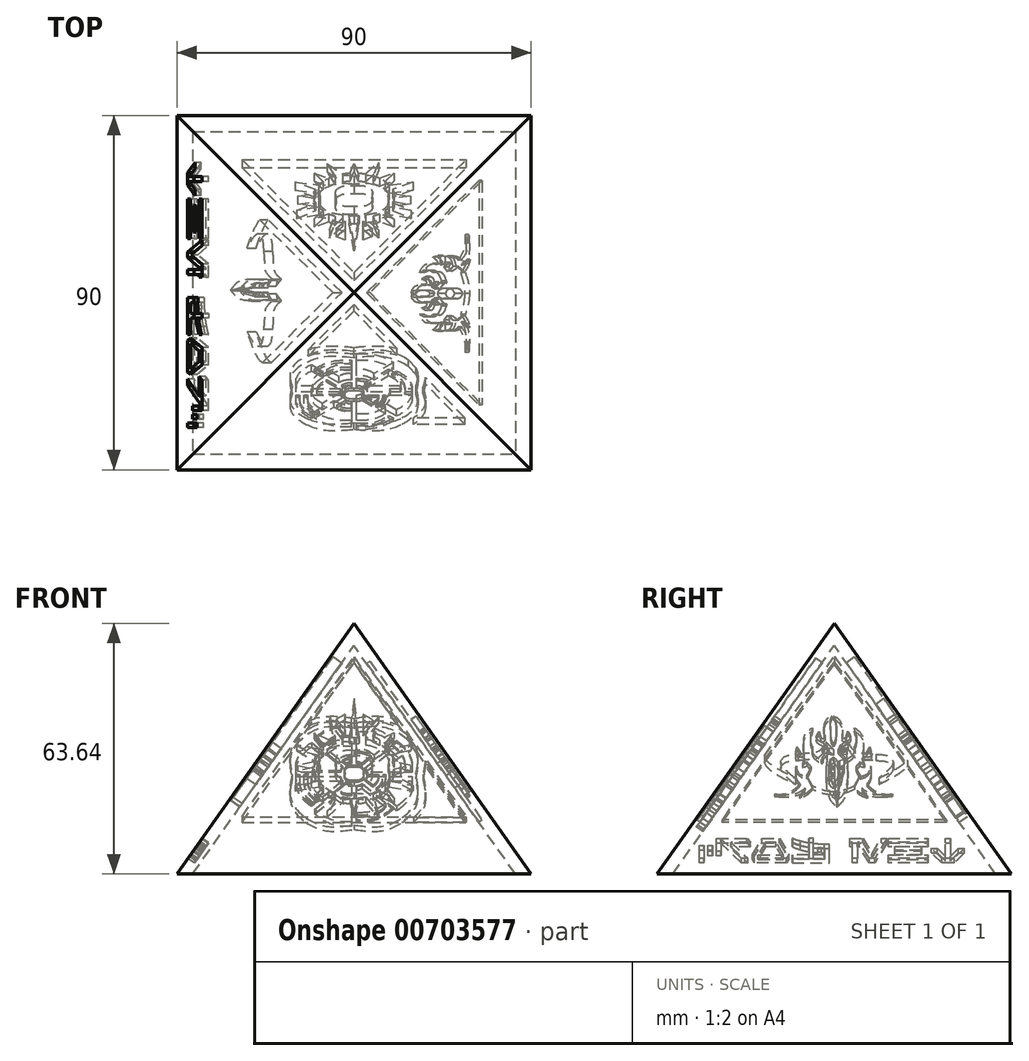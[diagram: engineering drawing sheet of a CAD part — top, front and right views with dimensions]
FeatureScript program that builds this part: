
annotation { "Feature Type Name" : "Feature", "Feature Type Description" : "" }
export const myFeature = defineFeature(function(context is Context, id is Id, definition is map)
    precondition{}
    {
        {
            var Q0;
            Q0=qCreatedBy(makeId("Top.planeOp"),FACE);
            cPlane(context, id + "F0", {"entities" : qUnion([Q0]), "cplaneType" : CPlaneType.OFFSET, "offset" : 63.64 * mm, "width" : 150 * mm, "height" : 150 * mm});
        }
        {
            var Q0;
            Q0=qCreatedBy(id+"F0.planeOp",FACE);
            var sketch = newSketch(context, id + "F1", { "sketchPlane" : qUnion([Q0])});
            skPoint(sketch, "E0", {"position": v(0, 0) * mm});
            skLineSegment(sketch, "E1.bottom", {"start": v(-47.05, 40.97) * mm, "end": v(62.4, 40.97) * mm});
            skLineSegment(sketch, "E1.top", {"start": v(-47.05, -49.65) * mm, "end": v(62.4, -49.65) * mm});
            skLineSegment(sketch, "E1.left", {"start": v(-47.05, 40.97) * mm, "end": v(-47.05, -49.65) * mm});
            skLineSegment(sketch, "E1.right", {"start": v(62.4, 40.97) * mm, "end": v(62.4, -49.65) * mm});
            skSolve(sketch);
        }
        {
            var Q0;
            Q0=qCreatedBy(makeId("Top.planeOp"),FACE);
            var sketch = newSketch(context, id + "F2", { "sketchPlane" : qUnion([Q0])});
            skLineSegment(sketch, "E2.bottom", {"start": v(-45, 45) * mm, "end": v(45, 45) * mm});
            skLineSegment(sketch, "E2.top", {"start": v(-45, -45) * mm, "end": v(45, -45) * mm});
            skLineSegment(sketch, "E2.left", {"start": v(-45, 45) * mm, "end": v(-45, -45) * mm});
            skLineSegment(sketch, "E2.right", {"start": v(45, 45) * mm, "end": v(45, -45) * mm});
            skPoint(sketch, "E3.orphan", {"position": v(-45, 0) * mm});
            skPoint(sketch, "E4.start.orphan", {"position": v(45, 0) * mm});
            skPoint(sketch, "E5.end.orphan", {"position": v(0, -45) * mm});
            skPoint(sketch, "E5.start.orphan", {"position": v(0, 45) * mm});
            skSolve(sketch);
        }
        {
            var Q0;
            Q0=makeQuery(id+"F2.imprint","IMPRINT",FACE,{"disambiguationData":[TD([[makeQuery(id+"F2.imprint","IMPRINT",EDGE,{"derivedFrom":sQuery(id+"F2.wireOp",EDGE,"E2.bottom")}),-1.0]])]});
            var Q1;
            Q1=sQuery(id+"F1.wireOp",VERTEX,"E0");
            loft(context, id + "F3", {"sheetProfilesArray" : [{ "sheetProfileEntities" : qUnion([Q0]) }, { "sheetProfileEntities" : qUnion([Q1]) }]});
        }
        {
            var Q0;
            Q0=qCreatedBy(makeId("Top.planeOp"),FACE);
            cPlane(context, id + "F4", {"entities" : qUnion([Q0]), "cplaneType" : CPlaneType.OFFSET, "offset" : 58 * mm, "width" : 150 * mm, "height" : 150 * mm});
        }
        {
            var Q0;
            Q0=qCreatedBy(id+"F4.planeOp",FACE);
            var sketch = newSketch(context, id + "F5", { "sketchPlane" : qUnion([Q0])});
            skPoint(sketch, "E6", {"position": v(0, 0) * mm});
            skSolve(sketch);
        }
        {
            var Q0;
            Q0=makeQuery(id+"F2.imprint","IMPRINT",FACE,{"disambiguationData":[TD([[makeQuery(id+"F2.imprint","IMPRINT",EDGE,{"derivedFrom":sQuery(id+"F2.wireOp",EDGE,"E2.bottom")}),-1.0]])]});
            var sketch = newSketch(context, id + "F6", { "sketchPlane" : qUnion([Q0])});
            skLineSegment(sketch, "E7.0", {"start": v(-41, 41) * mm, "end": v(-41, -41) * mm});
            skLineSegment(sketch, "E7.1", {"start": v(-41, 41) * mm, "end": v(41, 41) * mm});
            skLineSegment(sketch, "E7.2", {"start": v(41, 41) * mm, "end": v(41, -41) * mm});
            skLineSegment(sketch, "E7.3", {"start": v(-41, -41) * mm, "end": v(41, -41) * mm});
            skSolve(sketch);
        }
        {
            var Q1;
            Q1=makeQuery(id+"F6.imprint","IMPRINT",FACE,{"disambiguationData":[TD([[makeQuery(id+"F6.imprint","IMPRINT",EDGE,{"derivedFrom":sQuery(id+"F6.wireOp",EDGE,"E7.0")}),1.0]])]});
            var Q2;
            Q2=sQuery(id+"F5.wireOp",VERTEX,"E6");
            loft(context, id + "F7", {"operationType" : NewBodyOperationType.REMOVE, "sheetProfilesArray" : [{ "sheetProfileEntities" : qUnion([Q1]) }, { "sheetProfileEntities" : qUnion([Q2]) }]});
        }
        {
            var Q0;
            Q0=makeQuery(id+"F3.opLoft","SWEPT_FACE",FACE,{"disambiguationData":[OSD([sQuery(id+"F2.wireOp",EDGE,"E2.bottom"),sQuery(id+"F2.wireOp",EDGE,"E2.top"),sQuery(id+"F2.wireOp",EDGE,"E2.left")])]});
            var sketch = newSketch(context, id + "F8", { "sketchPlane" : qUnion([Q0])});
            skLineSegment(sketch, "E8", {"start": v(-30.48, -21.2) * mm, "end": v(-27.31, -21.2) * mm});
            skLineSegment(sketch, "E9", {"start": v(-27.31, -21.2) * mm, "end": v(-24.66, -18.07) * mm});
            skLineSegment(sketch, "E10", {"start": v(-24.66, -18.07) * mm, "end": v(-26.25, -18.07) * mm});
            skLineSegment(sketch, "E11", {"start": v(-26.25, -18.07) * mm, "end": v(-28.3, -20.5) * mm});
            skLineSegment(sketch, "E12", {"start": v(-28.3, -20.5) * mm, "end": v(-28.3, -14.95) * mm});
            skLineSegment(sketch, "E13", {"start": v(-28.3, -14.95) * mm, "end": v(-29.48, -14.95) * mm});
            skLineSegment(sketch, "E14", {"start": v(-29.48, -14.95) * mm, "end": v(-29.48, -20.5) * mm});
            skLineSegment(sketch, "E15", {"start": v(-29.48, -20.5) * mm, "end": v(-31.54, -18.07) * mm});
            skLineSegment(sketch, "E16", {"start": v(-31.54, -18.07) * mm, "end": v(-33.13, -18.07) * mm});
            skLineSegment(sketch, "E17", {"start": v(-33.13, -18.07) * mm, "end": v(-30.48, -21.2) * mm});
            skLineSegment(sketch, "E18", {"start": v(-13.74, -16.13) * mm, "end": v(-13.74, -14.95) * mm});
            skLineSegment(sketch, "E19", {"start": v(-13.74, -14.95) * mm, "end": v(-23.85, -14.95) * mm});
            skLineSegment(sketch, "E20", {"start": v(-23.85, -14.95) * mm, "end": v(-23.85, -16.13) * mm});
            skLineSegment(sketch, "E21", {"start": v(-23.85, -16.13) * mm, "end": v(-13.74, -16.13) * mm});
            skLineSegment(sketch, "E22", {"start": v(-13.74, -21.2) * mm, "end": v(-13.74, -20.01) * mm});
            skLineSegment(sketch, "E23", {"start": v(-13.74, -20.01) * mm, "end": v(-23.85, -20.01) * mm});
            skLineSegment(sketch, "E24", {"start": v(-23.85, -20.01) * mm, "end": v(-23.85, -21.2) * mm});
            skLineSegment(sketch, "E25", {"start": v(-23.85, -21.2) * mm, "end": v(-13.74, -21.2) * mm});
            skLineSegment(sketch, "E26", {"start": v(-15.46, -18.66) * mm, "end": v(-15.46, -17.48) * mm});
            skLineSegment(sketch, "E27", {"start": v(-15.46, -17.48) * mm, "end": v(-22.13, -17.48) * mm});
            skLineSegment(sketch, "E28", {"start": v(-22.13, -17.48) * mm, "end": v(-22.13, -18.66) * mm});
            skLineSegment(sketch, "E29", {"start": v(-22.13, -18.66) * mm, "end": v(-15.46, -18.66) * mm});
            skLineSegment(sketch, "E30", {"start": v(-9.62, -19.72) * mm, "end": v(-11.96, -14.95) * mm});
            skLineSegment(sketch, "E31", {"start": v(-11.96, -14.95) * mm, "end": v(-13.4, -14.95) * mm});
            skLineSegment(sketch, "E32", {"start": v(-13.4, -14.95) * mm, "end": v(-10.33, -21.2) * mm});
            skLineSegment(sketch, "E33", {"start": v(-10.33, -21.2) * mm, "end": v(-8.9, -21.2) * mm});
            skLineSegment(sketch, "E34", {"start": v(-8.9, -21.2) * mm, "end": v(-6.42, -16.13) * mm});
            skLineSegment(sketch, "E35", {"start": v(-6.42, -16.13) * mm, "end": v(-5.84, -16.13) * mm});
            skLineSegment(sketch, "E36", {"start": v(-5.84, -16.13) * mm, "end": v(-5.84, -21.2) * mm});
            skLineSegment(sketch, "E37", {"start": v(-5.84, -21.2) * mm, "end": v(-4.66, -21.2) * mm});
            skLineSegment(sketch, "E38", {"start": v(-4.66, -21.2) * mm, "end": v(-4.66, -16.13) * mm});
            skLineSegment(sketch, "E39", {"start": v(-4.66, -16.13) * mm, "end": v(-3.94, -16.13) * mm});
            skLineSegment(sketch, "E40", {"start": v(-3.94, -16.13) * mm, "end": v(-3.94, -14.95) * mm});
            skLineSegment(sketch, "E41", {"start": v(-3.94, -14.95) * mm, "end": v(-7.28, -14.95) * mm});
            skLineSegment(sketch, "E42", {"start": v(-7.28, -14.95) * mm, "end": v(-9.62, -19.72) * mm});
            skLineSegment(sketch, "E43", {"start": v(2.43, -20.01) * mm, "end": v(5.3, -20.01) * mm});
            skLineSegment(sketch, "E44", {"start": v(5.3, -20.01) * mm, "end": v(5.3, -17.82) * mm});
            skLineSegment(sketch, "E45", {"start": v(2.43, -17.95) * mm, "end": v(2.43, -20.01) * mm});
            skLineSegment(sketch, "E46", {"start": v(5.3, -16.6) * mm, "end": v(5.3, -14.95) * mm});
            skLineSegment(sketch, "E47", {"start": v(5.3, -14.95) * mm, "end": v(6.48, -14.95) * mm});
            skLineSegment(sketch, "E48", {"start": v(6.48, -14.95) * mm, "end": v(6.48, -16.4) * mm});
            skLineSegment(sketch, "E49", {"start": v(10.66, -14.95) * mm, "end": v(10.66, -16.14) * mm});
            skLineSegment(sketch, "E50", {"start": v(6.48, -17.65) * mm, "end": v(6.48, -20.01) * mm});
            skLineSegment(sketch, "E51", {"start": v(6.48, -20.01) * mm, "end": v(10.66, -20.01) * mm});
            skLineSegment(sketch, "E52", {"start": v(10.66, -20.01) * mm, "end": v(10.66, -21.2) * mm});
            skLineSegment(sketch, "E53", {"start": v(10.66, -21.2) * mm, "end": v(1.25, -21.2) * mm});
            skLineSegment(sketch, "E54", {"start": v(1.25, -21.2) * mm, "end": v(1.25, -16.76) * mm});
            skLineSegment(sketch, "E55", {"start": v(1.25, -16.76) * mm, "end": v(2.43, -16.76) * mm});
            skLineSegment(sketch, "E56", {"start": v(12.92, -20.01) * mm, "end": v(14.82, -16.13) * mm});
            skLineSegment(sketch, "E57", {"start": v(14.82, -16.13) * mm, "end": v(17.48, -16.13) * mm});
            skLineSegment(sketch, "E58", {"start": v(17.48, -16.13) * mm, "end": v(19.37, -20.01) * mm});
            skLineSegment(sketch, "E59", {"start": v(19.37, -20.01) * mm, "end": v(12.92, -20.01) * mm});
            skLineSegment(sketch, "E60", {"start": v(20.26, -21.2) * mm, "end": v(20.83, -20.04) * mm});
            skLineSegment(sketch, "E61", {"start": v(20.83, -20.04) * mm, "end": v(18.33, -14.95) * mm});
            skLineSegment(sketch, "E62", {"start": v(18.33, -14.95) * mm, "end": v(13.96, -14.95) * mm});
            skLineSegment(sketch, "E63", {"start": v(13.96, -14.95) * mm, "end": v(11.5, -19.98) * mm});
            skLineSegment(sketch, "E64", {"start": v(11.5, -19.98) * mm, "end": v(12.09, -21.2) * mm});
            skLineSegment(sketch, "E65", {"start": v(12.09, -21.2) * mm, "end": v(20.26, -21.2) * mm});
            skLineSegment(sketch, "E66", {"start": v(23.56, -21.2) * mm, "end": v(28.74, -15.1) * mm});
            skLineSegment(sketch, "E67", {"start": v(28.86, -14.95) * mm, "end": v(22.22, -14.95) * mm});
            skLineSegment(sketch, "E68", {"start": v(22.22, -14.95) * mm, "end": v(21.22, -16.13) * mm});
            skLineSegment(sketch, "E69", {"start": v(21.22, -16.13) * mm, "end": v(26.26, -16.13) * mm});
            skLineSegment(sketch, "E70", {"start": v(26.26, -16.13) * mm, "end": v(21.97, -21.2) * mm});
            skLineSegment(sketch, "E71", {"start": v(21.97, -21.2) * mm, "end": v(23.56, -21.2) * mm});
            skLineSegment(sketch, "E72", {"start": v(29.92, -19) * mm, "end": v(29.92, -14.95) * mm});
            skLineSegment(sketch, "E73", {"start": v(29.92, -14.95) * mm, "end": v(28.74, -14.95) * mm});
            skLineSegment(sketch, "E74", {"start": v(28.74, -15.1) * mm, "end": v(28.74, -19) * mm});
            skLineSegment(sketch, "E75", {"start": v(28.74, -19) * mm, "end": v(29.92, -19) * mm});
            skLineSegment(sketch, "E76", {"start": v(34.22, -21.2) * mm, "end": v(34.22, -17.13) * mm});
            skLineSegment(sketch, "E77", {"start": v(34.22, -17.13) * mm, "end": v(33.04, -17.13) * mm});
            skLineSegment(sketch, "E78", {"start": v(33.04, -17.13) * mm, "end": v(33.04, -21.2) * mm});
            skLineSegment(sketch, "E79", {"start": v(33.04, -21.2) * mm, "end": v(34.22, -21.2) * mm});
            skLineSegment(sketch, "E80", {"start": v(32.07, -19) * mm, "end": v(32.07, -17.13) * mm});
            skLineSegment(sketch, "E81", {"start": v(32.07, -17.13) * mm, "end": v(30.89, -17.13) * mm});
            skLineSegment(sketch, "E82", {"start": v(30.89, -17.13) * mm, "end": v(30.89, -19) * mm});
            skLineSegment(sketch, "E83", {"start": v(30.89, -19) * mm, "end": v(32.07, -19) * mm});
            skFitSpline(sketch, "E84", {"points": [v(5.3, -17.82) * mm, v(5.1, -17.85) * mm, v(4.72, -17.9) * mm, v(4.34, -17.92) * mm, v(4.16, -17.93) * mm]});
            skFitSpline(sketch, "E85", {"points": [v(4.16, -17.93) * mm, v(4, -17.94) * mm, v(3.7, -17.95) * mm, v(3.4, -17.96) * mm, v(3.25, -17.96) * mm]});
            skFitSpline(sketch, "E86", {"points": [v(3.25, -17.96) * mm, v(3.1, -17.97) * mm, v(2.83, -17.97) * mm, v(2.56, -17.96) * mm, v(2.43, -17.95) * mm]});
            skFitSpline(sketch, "E87", {"points": [v(2.43, -16.76) * mm, v(2.56, -16.77) * mm, v(2.82, -16.78) * mm, v(3.1, -16.78) * mm, v(3.23, -16.77) * mm]});
            skFitSpline(sketch, "E88", {"points": [v(3.23, -16.77) * mm, v(3.37, -16.77) * mm, v(3.67, -16.76) * mm, v(3.98, -16.74) * mm, v(4.14, -16.73) * mm]});
            skFitSpline(sketch, "E89", {"points": [v(4.14, -16.73) * mm, v(4.33, -16.71) * mm, v(4.71, -16.68) * mm, v(5.1, -16.63) * mm, v(5.3, -16.6) * mm]});
            skFitSpline(sketch, "E90", {"points": [v(6.48, -16.4) * mm, v(6.81, -16.33) * mm, v(7.5, -16.18) * mm, v(8.18, -15.97) * mm, v(8.52, -15.86) * mm]});
            skFitSpline(sketch, "E91", {"points": [v(8.52, -15.86) * mm, v(8.88, -15.74) * mm, v(9.62, -15.48) * mm, v(10.3, -15.13) * mm, v(10.66, -14.95) * mm]});
            skFitSpline(sketch, "E92", {"points": [v(10.66, -16.14) * mm, v(10.33, -16.3) * mm, v(9.66, -16.64) * mm, v(8.96, -16.92) * mm, v(8.6, -17.05) * mm]});
            skFitSpline(sketch, "E93", {"points": [v(8.6, -17.05) * mm, v(8.25, -17.18) * mm, v(7.56, -17.42) * mm, v(6.84, -17.57) * mm, v(6.48, -17.65) * mm]});
            skSolve(sketch);
        }
        {
            var Q0;
            {var subQ3=sQuery(id+"F8.wireOp",EDGE,"E72");Q0=makeQuery(id+"F8.imprint","IMPRINT",FACE,{"disambiguationData":[TD([[makeQuery(id+"F8.imprint","IMPRINT",EDGE,{"derivedFrom":subQ3}),1.0]])]});}
            var Q1;
            Q1=makeQuery(id+"F8.imprint","IMPRINT",FACE,{"disambiguationData":[TD([[makeQuery(id+"F8.imprint","IMPRINT",EDGE,{"derivedFrom":sQuery(id+"F8.wireOp",EDGE,"E80")}),1.0]])]});
            var Q2;
            Q2=makeQuery(id+"F8.imprint","IMPRINT",FACE,{"disambiguationData":[TD([[makeQuery(id+"F8.imprint","IMPRINT",EDGE,{"derivedFrom":sQuery(id+"F8.wireOp",EDGE,"E76")}),1.0]])]});
            var Q3;
            Q3=makeQuery(id+"F8.imprint","IMPRINT",FACE,{"disambiguationData":[TD([[makeQuery(id+"F8.imprint","IMPRINT",EDGE,{"derivedFrom":sQuery(id+"F8.wireOp",EDGE,"E56")}),1.0]])]});
            var Q4;
            Q4=makeQuery(id+"F8.imprint","IMPRINT",FACE,{"disambiguationData":[TD([[makeQuery(id+"F8.imprint","IMPRINT",EDGE,{"derivedFrom":sQuery(id+"F8.wireOp",EDGE,"E43")}),-1.0]])]});
            var Q5;
            Q5=makeQuery(id+"F8.imprint","IMPRINT",FACE,{"disambiguationData":[TD([[makeQuery(id+"F8.imprint","IMPRINT",EDGE,{"derivedFrom":sQuery(id+"F8.wireOp",EDGE,"E30")}),1.0]])]});
            var Q6;
            Q6=makeQuery(id+"F8.imprint","IMPRINT",FACE,{"disambiguationData":[TD([[makeQuery(id+"F8.imprint","IMPRINT",EDGE,{"derivedFrom":sQuery(id+"F8.wireOp",EDGE,"E18")}),1.0]])]});
            var Q7;
            Q7=makeQuery(id+"F8.imprint","IMPRINT",FACE,{"disambiguationData":[TD([[makeQuery(id+"F8.imprint","IMPRINT",EDGE,{"derivedFrom":sQuery(id+"F8.wireOp",EDGE,"E26")}),1.0]])]});
            var Q8;
            Q8=makeQuery(id+"F8.imprint","IMPRINT",FACE,{"disambiguationData":[TD([[makeQuery(id+"F8.imprint","IMPRINT",EDGE,{"derivedFrom":sQuery(id+"F8.wireOp",EDGE,"E22")}),1.0]])]});
            var Q9;
            Q9=makeQuery(id+"F8.imprint","IMPRINT",FACE,{"disambiguationData":[TD([[makeQuery(id+"F8.imprint","IMPRINT",EDGE,{"derivedFrom":sQuery(id+"F8.wireOp",EDGE,"E8")}),1.0]])]});
            extrude(context, id + "F9", {"entities" : qUnion([Q0, Q1, Q2, Q3, Q4, Q5, Q6, Q7, Q8, Q9]), "operationType" : NewBodyOperationType.REMOVE, "oppositeDirection" : true, "depth" : 2 * mm, "offsetDistance" : 25 * mm});
        }
        {
            var Q0;
            Q0=makeQuery(id+"F7.boolean.opBoolean","COPY",FACE,{"derivedFrom":makeQuery(id+"F7.opLoft","SWEPT_FACE",FACE,{"disambiguationData":[OSD([sQuery(id+"F6.wireOp",EDGE,"E7.0"),sQuery(id+"F6.wireOp",EDGE,"E7.1"),sQuery(id+"F6.wireOp",EDGE,"E7.2")])]})});
            var sketch = newSketch(context, id + "F10", { "sketchPlane" : qUnion([Q0])});
            skLineSegment(sketch, "E94", {"start": v(-41, -23.67) * mm, "end": v(0, 47.36) * mm, "construction": true});
            skLineSegment(sketch, "E95", {"start": v(0, 47.36) * mm, "end": v(41, -23.67) * mm, "construction": true});
            skLineSegment(sketch, "E96", {"start": v(41, -23.67) * mm, "end": v(-41, -23.67) * mm, "construction": true});
            skLineSegment(sketch, "E97.0", {"start": v(0, 42.02) * mm, "end": v(28.45, -7.63) * mm});
            skLineSegment(sketch, "E98", {"start": v(-28.45, -7.63) * mm, "end": v(28.45, -7.63) * mm});
            skLineSegment(sketch, "E99.trimOffspring", {"start": v(-28.45, -7.63) * mm, "end": v(0, 42.02) * mm});
            skFitSpline(sketch, "E100", {"points": [v(-1.26, 16.9) * mm, v(-0.84, 16.96) * mm, v(-0.42, 16.99) * mm, v(0.01, 16.99) * mm]});
            skFitSpline(sketch, "E101", {"points": [v(0, 16.99) * mm, v(0.42, 17) * mm, v(0.84, 16.97) * mm, v(1.25, 16.91) * mm]});
            skLineSegment(sketch, "E102", {"start": v(0, 29.1) * mm, "end": v(-1.06, 18.9) * mm});
            skLineSegment(sketch, "E103", {"start": v(1.05, 18.88) * mm, "end": v(0, 29.1) * mm});
            skLineSegment(sketch, "E104", {"start": v(-2.27, 24.2) * mm, "end": v(-4.53, 22.69) * mm});
            skLineSegment(sketch, "E105", {"start": v(-4.53, 22.69) * mm, "end": v(-2.27, 19.3) * mm});
            skLineSegment(sketch, "E106", {"start": v(-2.27, 19.3) * mm, "end": v(-2.27, 24.2) * mm});
            skLineSegment(sketch, "E107", {"start": v(2.27, 24.2) * mm, "end": v(2.27, 19.3) * mm});
            skLineSegment(sketch, "E108", {"start": v(2.27, 19.3) * mm, "end": v(4.53, 22.69) * mm});
            skLineSegment(sketch, "E109", {"start": v(4.53, 22.69) * mm, "end": v(2.27, 24.2) * mm});
            skFitSpline(sketch, "E110", {"points": [v(-4.87, 17.28) * mm, v(-5.41, 16.99) * mm, v(-5.93, 16.64) * mm, v(-6.4, 16.26) * mm]});
            skLineSegment(sketch, "E111", {"start": v(-6.22, 23.35) * mm, "end": v(-4.87, 17.28) * mm});
            skFitSpline(sketch, "E112", {"points": [v(-7.9, 14.76) * mm, v(-8.3, 14.28) * mm, v(-8.66, 13.76) * mm, v(-8.96, 13.2) * mm]});
            skLineSegment(sketch, "E113", {"start": v(-6.4, 16.26) * mm, "end": v(-10.15, 18.49) * mm});
            skLineSegment(sketch, "E114", {"start": v(-10.15, 18.49) * mm, "end": v(-7.9, 14.76) * mm});
            skFitSpline(sketch, "E115", {"points": [v(-9.78, 11.23) * mm, v(-9.96, 10.64) * mm, v(-10.08, 10.02) * mm, v(-10.15, 9.39) * mm]});
            skLineSegment(sketch, "E116", {"start": v(-8.96, 13.2) * mm, "end": v(-14.62, 14.72) * mm});
            skLineSegment(sketch, "E117", {"start": v(-14.62, 14.72) * mm, "end": v(-9.78, 11.23) * mm});
            skFitSpline(sketch, "E118", {"points": [v(-10.15, 7.28) * mm, v(-10.08, 6.66) * mm, v(-9.96, 6.05) * mm, v(-9.78, 5.46) * mm]});
            skLineSegment(sketch, "E119", {"start": v(-10.15, 9.39) * mm, "end": v(-14.35, 8.34) * mm});
            skLineSegment(sketch, "E120", {"start": v(-14.35, 8.34) * mm, "end": v(-10.15, 7.28) * mm});
            skFitSpline(sketch, "E121", {"points": [v(-8.96, 3.46) * mm, v(-8.66, 2.91) * mm, v(-8.3, 2.4) * mm, v(-7.9, 1.91) * mm]});
            skLineSegment(sketch, "E122", {"start": v(-9.78, 5.46) * mm, "end": v(-15, 2.13) * mm});
            skLineSegment(sketch, "E123", {"start": v(-15, 2.13) * mm, "end": v(-8.96, 3.46) * mm});
            skFitSpline(sketch, "E124", {"points": [v(-6.42, 0.43) * mm, v(-5.94, 0.04) * mm, v(-5.42, -0.3) * mm, v(-4.87, -0.6) * mm]});
            skLineSegment(sketch, "E125", {"start": v(-7.9, 1.91) * mm, "end": v(-10.15, -1.8) * mm});
            skLineSegment(sketch, "E126", {"start": v(-10.15, -1.8) * mm, "end": v(-6.42, 0.43) * mm});
            skFitSpline(sketch, "E127", {"points": [v(-2.89, -1.43) * mm, v(-2.3, -1.61) * mm, v(-1.68, -1.73) * mm, v(-1.05, -1.8) * mm]});
            skLineSegment(sketch, "E128", {"start": v(-4.87, -0.6) * mm, "end": v(-6.88, -6.06) * mm});
            skLineSegment(sketch, "E129", {"start": v(-6.88, -6.06) * mm, "end": v(-2.89, -1.43) * mm});
            skFitSpline(sketch, "E130", {"points": [v(1.05, -1.8) * mm, v(1.68, -1.74) * mm, v(2.3, -1.61) * mm, v(2.9, -1.43) * mm]});
            skLineSegment(sketch, "E131", {"start": v(-1.05, -1.8) * mm, "end": v(0, -6.01) * mm});
            skLineSegment(sketch, "E132", {"start": v(0, -6.01) * mm, "end": v(1.05, -1.8) * mm});
            skFitSpline(sketch, "E133", {"points": [v(4.88, -0.62) * mm, v(5.42, -0.32) * mm, v(5.94, 0.03) * mm, v(6.42, 0.42) * mm]});
            skLineSegment(sketch, "E134", {"start": v(2.9, -1.43) * mm, "end": v(6.18, -6.4) * mm});
            skLineSegment(sketch, "E135", {"start": v(6.18, -6.4) * mm, "end": v(4.88, -0.62) * mm});
            skFitSpline(sketch, "E136", {"points": [v(7.92, 1.91) * mm, v(8.31, 2.4) * mm, v(8.66, 2.91) * mm, v(8.96, 3.46) * mm]});
            skLineSegment(sketch, "E137", {"start": v(6.42, 0.42) * mm, "end": v(10.15, -1.8) * mm});
            skLineSegment(sketch, "E138", {"start": v(10.15, -1.8) * mm, "end": v(7.92, 1.91) * mm});
            skFitSpline(sketch, "E139", {"points": [v(9.78, 5.46) * mm, v(9.96, 6.05) * mm, v(10.08, 6.66) * mm, v(10.15, 7.28) * mm]});
            skLineSegment(sketch, "E140", {"start": v(8.96, 3.46) * mm, "end": v(15, 2.13) * mm});
            skLineSegment(sketch, "E141", {"start": v(15, 2.13) * mm, "end": v(9.78, 5.46) * mm});
            skFitSpline(sketch, "E142", {"points": [v(10.15, 9.39) * mm, v(10.08, 10.02) * mm, v(9.96, 10.64) * mm, v(9.78, 11.23) * mm]});
            skLineSegment(sketch, "E143", {"start": v(10.15, 7.28) * mm, "end": v(14.35, 8.34) * mm});
            skLineSegment(sketch, "E144", {"start": v(14.35, 8.34) * mm, "end": v(10.15, 9.39) * mm});
            skFitSpline(sketch, "E145", {"points": [v(8.96, 13.2) * mm, v(8.66, 13.76) * mm, v(8.3, 14.29) * mm, v(7.9, 14.77) * mm]});
            skLineSegment(sketch, "E146", {"start": v(9.78, 11.23) * mm, "end": v(14.52, 14.7) * mm});
            skLineSegment(sketch, "E147", {"start": v(14.52, 14.7) * mm, "end": v(8.96, 13.2) * mm});
            skFitSpline(sketch, "E148", {"points": [v(6.42, 16.26) * mm, v(5.94, 16.65) * mm, v(5.42, 16.98) * mm, v(4.88, 17.28) * mm]});
            skLineSegment(sketch, "E149", {"start": v(7.9, 14.77) * mm, "end": v(10.15, 18.49) * mm});
            skLineSegment(sketch, "E150", {"start": v(10.15, 18.49) * mm, "end": v(6.42, 16.26) * mm});
            skFitSpline(sketch, "E151", {"points": [v(2.89, 16.5) * mm, v(6.25, 15.31) * mm, v(8.66, 12.1) * mm, v(8.66, 8.34) * mm]});
            skFitSpline(sketch, "E152", {"points": [v(8.66, 8.34) * mm, v(8.66, 3.56) * mm, v(4.8, -0.32) * mm, v(0.01, -0.32) * mm]});
            skFitSpline(sketch, "E153", {"points": [v(0.01, -0.32) * mm, v(-4.77, -0.32) * mm, v(-8.66, 3.56) * mm, v(-8.66, 8.34) * mm]});
            skFitSpline(sketch, "E154", {"points": [v(-8.66, 8.34) * mm, v(-8.66, 12.1) * mm, v(-6.25, 15.3) * mm, v(-2.89, 16.48) * mm]});
            skLineSegment(sketch, "E155", {"start": v(4.88, 17.28) * mm, "end": v(6.22, 23.35) * mm});
            skLineSegment(sketch, "E156", {"start": v(6.22, 23.35) * mm, "end": v(2.89, 18.12) * mm});
            skLineSegment(sketch, "E157", {"start": v(2.89, 18.12) * mm, "end": v(2.89, 16.5) * mm});
            skFitSpline(sketch, "E158", {"points": [v(0, 12.87) * mm, v(-2.5, 12.87) * mm, v(-4.53, 10.84) * mm, v(-4.53, 8.34) * mm]});
            skFitSpline(sketch, "E159", {"points": [v(-4.53, 8.34) * mm, v(-4.53, 5.83) * mm, v(-2.5, 3.8) * mm, v(0, 3.8) * mm]});
            skFitSpline(sketch, "E160", {"points": [v(0, 3.8) * mm, v(2.5, 3.8) * mm, v(4.53, 5.83) * mm, v(4.53, 8.34) * mm]});
            skFitSpline(sketch, "E161", {"points": [v(4.53, 8.34) * mm, v(4.53, 10.84) * mm, v(2.5, 12.87) * mm, v(0, 12.87) * mm]});
            skLineSegment(sketch, "E162", {"start": v(-2.89, 16.48) * mm, "end": v(-2.89, 18.12) * mm});
            skLineSegment(sketch, "E163", {"start": v(-2.89, 18.12) * mm, "end": v(-6.22, 23.35) * mm});
            skLineSegment(sketch, "E164", {"start": v(-1.06, 18.9) * mm, "end": v(-1.26, 16.9) * mm});
            skLineSegment(sketch, "E165", {"start": v(1.05, 18.88) * mm, "end": v(1.25, 16.91) * mm});
            skSolve(sketch);
        }
        {
            var Q0;
            Q0=makeQuery(id+"F10.imprint","IMPRINT",FACE,{"disambiguationData":[TD([[makeQuery(id+"F10.imprint","IMPRINT",EDGE,{"derivedFrom":sQuery(id+"F10.wireOp",EDGE,"E115")}),-1.0]])]});
            var Q1;
            Q1=makeQuery(id+"F10.imprint","IMPRINT",FACE,{"disambiguationData":[TD([[makeQuery(id+"F10.imprint","IMPRINT",EDGE,{"derivedFrom":sQuery(id+"F10.wireOp",EDGE,"E133")}),-1.0]])]});
            var Q2;
            Q2=makeQuery(id+"F10.imprint","IMPRINT",FACE,{"disambiguationData":[TD([[makeQuery(id+"F10.imprint","IMPRINT",EDGE,{"derivedFrom":sQuery(id+"F10.wireOp",EDGE,"E127")}),-1.0]])]});
            var Q3;
            Q3=makeQuery(id+"F10.imprint","IMPRINT",FACE,{"disambiguationData":[TD([[makeQuery(id+"F10.imprint","IMPRINT",EDGE,{"derivedFrom":sQuery(id+"F10.wireOp",EDGE,"E104")}),-1.0]])]});
            extrude(context, id + "F11", {"entities" : qUnion([Q0, Q1, Q2, Q3]), "operationType" : NewBodyOperationType.REMOVE, "oppositeDirection" : true, "depth" : 2.5 * mm, "offsetDistance" : 25 * mm});
        }
        {
            var Q0;
            Q0=makeQuery(id+"F7.boolean.opBoolean","COPY",FACE,{"derivedFrom":makeQuery(id+"F7.opLoft","SWEPT_FACE",FACE,{"disambiguationData":[OSD([sQuery(id+"F6.wireOp",EDGE,"E7.0"),sQuery(id+"F6.wireOp",EDGE,"E7.1"),sQuery(id+"F6.wireOp",EDGE,"E7.3")])]})});
            var sketch = newSketch(context, id + "F12", { "sketchPlane" : qUnion([Q0])});
            skLineSegment(sketch, "E166", {"start": v(0, 47.36) * mm, "end": v(41, -23.67) * mm, "construction": true});
            skLineSegment(sketch, "E167", {"start": v(41, -23.67) * mm, "end": v(-41, -23.67) * mm, "construction": true});
            skLineSegment(sketch, "E168.0", {"start": v(0, 42.02) * mm, "end": v(28.45, -7.63) * mm});
            skLineSegment(sketch, "E169", {"start": v(-28.45, -7.63) * mm, "end": v(28.45, -7.63) * mm});
            skLineSegment(sketch, "E170.trimOffspring", {"start": v(-28.45, -7.63) * mm, "end": v(0, 42.02) * mm});
            skFitSpline(sketch, "E171", {"points": [v(-2.96, 21.4) * mm, v(-3.37, 21.37) * mm, v(-3.6, 21.2) * mm, v(-3.6, 20.86) * mm]});
            skFitSpline(sketch, "E172", {"points": [v(-3.6, 20.86) * mm, v(-3.6, 20.02) * mm, v(-2.1, 18.49) * mm, v(-0.2, 17.35) * mm]});
            skFitSpline(sketch, "E173", {"points": [v(-4.91, 20.37) * mm, v(-5.22, 20.4) * mm, v(-5.38, 19.99) * mm, v(-5.44, 19.59) * mm]});
            skFitSpline(sketch, "E174", {"points": [v(-5.44, 19.59) * mm, v(-5.98, 15.78) * mm, v(-7.7, 15.7) * mm, v(-8.98, 15.45) * mm]});
            skFitSpline(sketch, "E175", {"points": [v(-8.98, 15.45) * mm, v(-13.62, 14.55) * mm, v(-17.73, 11.22) * mm, v(-9.88, 4.16) * mm]});
            skFitSpline(sketch, "E176", {"points": [v(-9.88, 4.16) * mm, v(-13.57, 9.03) * mm, v(-12.2, 11.06) * mm, v(-9.21, 11.58) * mm]});
            skFitSpline(sketch, "E177", {"points": [v(-9.21, 11.58) * mm, v(-6.9, 11.98) * mm, v(-4, 12.53) * mm, v(-2.06, 15.37) * mm]});
            skLineSegment(sketch, "E178", {"start": v(-0.48, 14.3) * mm, "end": v(-4.91, 20.37) * mm});
            skFitSpline(sketch, "E179", {"points": [v(-1.78, 13.57) * mm, v(-1.57, 0.89) * mm, v(-0.04, -2.03) * mm, v(0.58, -2.7) * mm]});
            skFitSpline(sketch, "E180", {"points": [v(0.58, -2.7) * mm, v(0.63, -2.75) * mm, v(0.67, -2.8) * mm, v(0.7, -2.82) * mm]});
            skFitSpline(sketch, "E181", {"points": [v(0.7, -2.82) * mm, v(0.75, -2.8) * mm, v(0.79, -2.75) * mm, v(0.84, -2.7) * mm]});
            skFitSpline(sketch, "E182", {"points": [v(0.84, -2.7) * mm, v(1.46, -2.03) * mm, v(2.98, 0.9) * mm, v(3.2, 13.57) * mm]});
            skLineSegment(sketch, "E183", {"start": v(-2.06, 15.37) * mm, "end": v(-0.26, 13.12) * mm});
            skLineSegment(sketch, "E184", {"start": v(-0.26, 13.12) * mm, "end": v(-1.78, 13.57) * mm});
            skFitSpline(sketch, "E185", {"points": [v(3.48, 15.37) * mm, v(5.42, 12.53) * mm, v(8.32, 11.98) * mm, v(10.63, 11.58) * mm]});
            skFitSpline(sketch, "E186", {"points": [v(10.63, 11.58) * mm, v(13.62, 11.06) * mm, v(14.98, 9.03) * mm, v(11.3, 4.16) * mm]});
            skFitSpline(sketch, "E187", {"points": [v(11.3, 4.16) * mm, v(19.15, 11.22) * mm, v(15.04, 14.55) * mm, v(10.4, 15.45) * mm]});
            skFitSpline(sketch, "E188", {"points": [v(10.4, 15.45) * mm, v(9.12, 15.7) * mm, v(7.4, 15.78) * mm, v(6.85, 19.59) * mm]});
            skFitSpline(sketch, "E189", {"points": [v(6.85, 19.58) * mm, v(6.8, 19.98) * mm, v(6.64, 20.39) * mm, v(6.33, 20.37) * mm]});
            skLineSegment(sketch, "E190", {"start": v(3.2, 13.57) * mm, "end": v(1.67, 13.12) * mm});
            skLineSegment(sketch, "E191", {"start": v(1.67, 13.12) * mm, "end": v(3.48, 15.37) * mm});
            skFitSpline(sketch, "E192", {"points": [v(1.62, 17.35) * mm, v(3.52, 18.49) * mm, v(5.02, 20.02) * mm, v(5.02, 20.86) * mm]});
            skFitSpline(sketch, "E193", {"points": [v(5.02, 20.86) * mm, v(5.02, 21.25) * mm, v(4.71, 21.42) * mm, v(4.19, 21.4) * mm]});
            skFitSpline(sketch, "E194", {"points": [v(4.19, 21.4) * mm, v(3.52, 21.37) * mm, v(2.5, 21.02) * mm, v(1.36, 20.37) * mm]});
            skLineSegment(sketch, "E195", {"start": v(6.33, 20.37) * mm, "end": v(1.9, 14.3) * mm});
            skFitSpline(sketch, "E196", {"points": [v(0.05, 20.37) * mm, v(-1.08, 21.02) * mm, v(-2.1, 21.37) * mm, v(-2.77, 21.4) * mm]});
            skFitSpline(sketch, "E197", {"points": [v(-2.77, 21.4) * mm, v(-2.84, 21.4) * mm, v(-2.9, 21.4) * mm, v(-2.96, 21.4) * mm]});
            skLineSegment(sketch, "E198", {"start": v(1.36, 20.37) * mm, "end": v(1.36, 17.2) * mm});
            skLineSegment(sketch, "E199", {"start": v(1.36, 17.2) * mm, "end": v(1.36, 13.57) * mm});
            skLineSegment(sketch, "E200", {"start": v(1.36, 13.57) * mm, "end": v(1.36, 13.03) * mm});
            skLineSegment(sketch, "E201", {"start": v(1.36, 13.03) * mm, "end": v(0.05, 13.03) * mm});
            skLineSegment(sketch, "E202", {"start": v(0.05, 13.03) * mm, "end": v(0.05, 13.57) * mm});
            skLineSegment(sketch, "E203", {"start": v(0.05, 13.57) * mm, "end": v(0.05, 17.2) * mm});
            skLineSegment(sketch, "E204", {"start": v(0.05, 17.2) * mm, "end": v(0.05, 20.37) * mm});
            skFitSpline(sketch, "E205", {"points": [v(0.05, 9.55) * mm, v(0.06, 8.7) * mm, v(0.07, 7.94) * mm, v(0.09, 7.22) * mm]});
            skLineSegment(sketch, "E206", {"start": v(-1, 10.17) * mm, "end": v(0.05, 9.55) * mm});
            skLineSegment(sketch, "E207", {"start": v(0.09, 7.22) * mm, "end": v(-1, 8.08) * mm});
            skLineSegment(sketch, "E208", {"start": v(-1, 8.08) * mm, "end": v(-1, 10.17) * mm});
            skFitSpline(sketch, "E209", {"points": [v(1.33, 7.22) * mm, v(1.34, 7.94) * mm, v(1.36, 8.7) * mm, v(1.36, 9.55) * mm]});
            skLineSegment(sketch, "E210", {"start": v(2.4, 10.17) * mm, "end": v(2.4, 8.08) * mm});
            skLineSegment(sketch, "E211", {"start": v(2.4, 8.08) * mm, "end": v(1.33, 7.22) * mm});
            skLineSegment(sketch, "E212", {"start": v(1.36, 9.55) * mm, "end": v(2.4, 10.17) * mm});
            skFitSpline(sketch, "E213", {"points": [v(0.1, 6.68) * mm, v(0.05, 3.98) * mm, v(0.42, 1.05) * mm, v(0.58, -1.77) * mm]});
            skLineSegment(sketch, "E214", {"start": v(-1, 7.56) * mm, "end": v(0.1, 6.68) * mm});
            skFitSpline(sketch, "E215", {"points": [v(0.84, -1.77) * mm, v(1.1, 1.1) * mm, v(1.36, 3.98) * mm, v(1.32, 6.68) * mm]});
            skLineSegment(sketch, "E216", {"start": v(1.32, 6.68) * mm, "end": v(2.4, 7.56) * mm});
            skLineSegment(sketch, "E217", {"start": v(-1, 7.56) * mm, "end": v(0.58, -1.77) * mm});
            skLineSegment(sketch, "E218", {"start": v(0.84, -1.77) * mm, "end": v(2.4, 7.56) * mm});
            skLineSegment(sketch, "E219", {"start": v(0.05, 13.03) * mm, "end": v(-0.26, 13.12) * mm});
            skLineSegment(sketch, "E220", {"start": v(1.36, 13.03) * mm, "end": v(1.67, 13.12) * mm});
            skLineSegment(sketch, "E221", {"start": v(-0.48, 17.52) * mm, "end": v(-0.48, 14.3) * mm});
            skLineSegment(sketch, "E222", {"start": v(1.9, 17.52) * mm, "end": v(1.9, 14.3) * mm});
            skLineSegment(sketch, "E223", {"start": v(0, 47.36) * mm, "end": v(-41, -23.67) * mm, "construction": true});
            skSolve(sketch);
        }
        {
            var Q0;
            Q0=makeQuery(id+"F12.imprint","IMPRINT",FACE,{"disambiguationData":[TD([[makeQuery(id+"F12.imprint","IMPRINT",EDGE,{"derivedFrom":sQuery(id+"F12.wireOp",EDGE,"E171")}),1.0]])]});
            var Q1;
            Q1=makeQuery(id+"F12.imprint","IMPRINT",FACE,{"disambiguationData":[TD([[makeQuery(id+"F12.imprint","IMPRINT",EDGE,{"derivedFrom":sQuery(id+"F12.wireOp",EDGE,"E185")}),1.0]])]});
            var Q2;
            Q2=makeQuery(id+"F12.imprint","IMPRINT",FACE,{"disambiguationData":[TD([[makeQuery(id+"F12.imprint","IMPRINT",EDGE,{"derivedFrom":sQuery(id+"F12.wireOp",EDGE,"E179")}),1.0]])]});
            extrude(context, id + "F13", {"entities" : qUnion([Q0, Q1, Q2]), "operationType" : NewBodyOperationType.REMOVE, "oppositeDirection" : true, "depth" : 2.75 * mm, "offsetDistance" : 25 * mm});
        }
        {
            var Q0;
            Q0=makeQuery(id+"F7.boolean.opBoolean","COPY",FACE,{"derivedFrom":makeQuery(id+"F7.opLoft","SWEPT_FACE",FACE,{"disambiguationData":[OSD([sQuery(id+"F6.wireOp",EDGE,"E7.1"),sQuery(id+"F6.wireOp",EDGE,"E7.2"),sQuery(id+"F6.wireOp",EDGE,"E7.3")])]})});
            var sketch = newSketch(context, id + "F14", { "sketchPlane" : qUnion([Q0])});
            skLineSegment(sketch, "E224", {"start": v(-41, -23.67) * mm, "end": v(0, 47.36) * mm, "construction": true});
            skLineSegment(sketch, "E225", {"start": v(0, 47.36) * mm, "end": v(41, -23.67) * mm, "construction": true});
            skLineSegment(sketch, "E226", {"start": v(41, -23.67) * mm, "end": v(-41, -23.67) * mm, "construction": true});
            skLineSegment(sketch, "E227.0", {"start": v(0, 41.8) * mm, "end": v(28.51, -7.6) * mm});
            skLineSegment(sketch, "E228", {"start": v(-28.51, -7.6) * mm, "end": v(28.51, -7.6) * mm});
            skLineSegment(sketch, "E229.trimOffspring", {"start": v(-28.51, -7.6) * mm, "end": v(0, 41.8) * mm});
            skFitSpline(sketch, "E230", {"points": [v(8.78, -0.88) * mm, v(8.2, -0.15) * mm, v(7.74, 0.72) * mm, v(7.4, 1.66) * mm]});
            skFitSpline(sketch, "E231", {"points": [v(7.4, 1.66) * mm, v(8.79, 0.33) * mm, v(10.83, -0.52) * mm, v(13.1, -0.52) * mm]});
            skFitSpline(sketch, "E232", {"points": [v(13.1, -0.52) * mm, v(13.82, -0.52) * mm, v(14.53, -0.43) * mm, v(15.2, -0.27) * mm]});
            skFitSpline(sketch, "E233", {"points": [v(15.2, -0.27) * mm, v(12.68, -0.17) * mm, v(10.4, 1.02) * mm, v(8.65, 2.92) * mm]});
            skFitSpline(sketch, "E234", {"points": [v(8.65, 2.92) * mm, v(9.28, 3.83) * mm, v(9.69, 5.44) * mm, v(9.69, 7.27) * mm]});
            skFitSpline(sketch, "E235", {"points": [v(9.69, 7.27) * mm, v(9.69, 7.69) * mm, v(9.67, 8.09) * mm, v(9.63, 8.47) * mm]});
            skFitSpline(sketch, "E236", {"points": [v(9.63, 8.47) * mm, v(9.38, 6.97) * mm, v(8.38, 5.73) * mm, v(7.04, 5.17) * mm]});
            skFitSpline(sketch, "E237", {"points": [v(7.04, 5.17) * mm, v(6.56, 6.02) * mm, v(6.17, 6.96) * mm, v(5.88, 7.95) * mm]});
            skFitSpline(sketch, "E238", {"points": [v(5.88, 7.95) * mm, v(6.28, 8.37) * mm, v(6.62, 8.83) * mm, v(6.9, 9.33) * mm]});
            skFitSpline(sketch, "E239", {"points": [v(6.9, 9.33) * mm, v(7.25, 8.97) * mm, v(7.5, 8.73) * mm, v(8.01, 8.7) * mm]});
            skFitSpline(sketch, "E240", {"points": [v(8.01, 8.7) * mm, v(7.74, 10.92) * mm, v(9.44, 10.92) * mm, v(9.44, 14.09) * mm]});
            skFitSpline(sketch, "E241", {"points": [v(9.44, 14.09) * mm, v(8.96, 13.11) * mm, v(8.23, 11.9) * mm, v(7.73, 12.1) * mm]});
            skFitSpline(sketch, "E242", {"points": [v(7.73, 12.1) * mm, v(7.74, 12.24) * mm, v(7.74, 12.37) * mm, v(7.74, 12.5) * mm]});
            skFitSpline(sketch, "E243", {"points": [v(7.74, 12.5) * mm, v(7.74, 15.64) * mm, v(7.25, 18.23) * mm, v(5.55, 19.93) * mm]});
            skFitSpline(sketch, "E244", {"points": [v(5.55, 19.93) * mm, v(5.8, 18.71) * mm, v(6.04, 18.14) * mm, v(6.04, 16.86) * mm]});
            skFitSpline(sketch, "E245", {"points": [v(6.04, 16.86) * mm, v(6.04, 15.87) * mm, v(5.86, 14.93) * mm, v(5.55, 14.07) * mm]});
            skFitSpline(sketch, "E246", {"points": [v(5.55, 14.07) * mm, v(5.54, 12.48) * mm, v(4.67, 11.1) * mm, v(3.38, 10.18) * mm]});
            skFitSpline(sketch, "E247", {"points": [v(3.38, 10.18) * mm, v(3.1, 9.97) * mm, v(2.87, 10.19) * mm, v(3.09, 10.6) * mm]});
            skFitSpline(sketch, "E248", {"points": [v(3.09, 10.6) * mm, v(2.63, 11.4) * mm, v(2.14, 12.14) * mm, v(1.34, 13.15) * mm]});
            skFitSpline(sketch, "E249", {"points": [v(1.34, 13.15) * mm, v(1.51, 13.46) * mm, v(1.76, 14.2) * mm, v(1.9, 14.58) * mm]});
            skFitSpline(sketch, "E250", {"points": [v(1.9, 14.58) * mm, v(2.39, 14.33) * mm, v(2.87, 13.36) * mm, v(3.12, 13.6) * mm]});
            skFitSpline(sketch, "E251", {"points": [v(3.12, 13.53) * mm, v(2.39, 14.75) * mm, v(4.33, 16.45) * mm, v(3.85, 18.89) * mm]});
            skFitSpline(sketch, "E252", {"points": [v(3.85, 18.89) * mm, v(3.6, 17.91) * mm, v(3.12, 16.7) * mm, v(2.37, 17) * mm]});
            skFitSpline(sketch, "E253", {"points": [v(2.37, 17) * mm, v(2.38, 17.23) * mm, v(2.39, 17.45) * mm, v(2.39, 17.67) * mm]});
            skFitSpline(sketch, "E254", {"points": [v(2.39, 17.67) * mm, v(2.54, 20.43) * mm, v(1.74, 22.82) * mm, v(0.52, 23.62) * mm]});
            skFitSpline(sketch, "E255", {"points": [v(0.52, 23.63) * mm, v(0.9, 23.07) * mm, v(1.08, 21.4) * mm, v(0.93, 19.44) * mm]});
            skFitSpline(sketch, "E256", {"points": [v(0.93, 19.44) * mm, v(0.93, 17.48) * mm, v(0.62, 15.83) * mm, v(0.2, 15.3) * mm]});
            skFitSpline(sketch, "E257", {"points": [v(0.2, 15.3) * mm, v(-0.23, 15.83) * mm, v(-0.53, 17.48) * mm, v(-0.53, 19.44) * mm]});
            skFitSpline(sketch, "E258", {"points": [v(-0.53, 19.44) * mm, v(-0.54, 21.4) * mm, v(-0.23, 23.06) * mm, v(0.2, 23.58) * mm]});
            skFitSpline(sketch, "E259", {"points": [v(0.2, 23.58) * mm, v(-1.07, 22.84) * mm, v(-2, 20.5) * mm, v(-2, 17.74) * mm]});
            skFitSpline(sketch, "E260", {"points": [v(-2, 17.74) * mm, v(-2, 17.52) * mm, v(-2, 17.3) * mm, v(-1.98, 17.08) * mm]});
            skFitSpline(sketch, "E261", {"points": [v(-1.98, 17.08) * mm, v(-2.73, 16.76) * mm, v(-3.21, 17.98) * mm, v(-3.46, 18.96) * mm]});
            skFitSpline(sketch, "E262", {"points": [v(-3.46, 18.96) * mm, v(-3.94, 16.52) * mm, v(-2, 14.82) * mm, v(-2.73, 13.6) * mm]});
            skFitSpline(sketch, "E263", {"points": [v(-2.73, 13.6) * mm, v(-2.48, 13.36) * mm, v(-2, 14.33) * mm, v(-1.5, 14.58) * mm]});
            skFitSpline(sketch, "E264", {"points": [v(-1.5, 14.58) * mm, v(-1.37, 14.2) * mm, v(-1.12, 13.46) * mm, v(-0.95, 13.15) * mm]});
            skFitSpline(sketch, "E265", {"points": [v(-0.95, 13.15) * mm, v(-1.75, 12.14) * mm, v(-2.24, 11.4) * mm, v(-2.7, 10.6) * mm]});
            skFitSpline(sketch, "E266", {"points": [v(-2.7, 10.6) * mm, v(-2.48, 10.19) * mm, v(-2.7, 9.97) * mm, v(-3, 10.18) * mm]});
            skFitSpline(sketch, "E267", {"points": [v(-3, 10.18) * mm, v(-4.28, 11.1) * mm, v(-5.15, 12.48) * mm, v(-5.16, 14.07) * mm]});
            skFitSpline(sketch, "E268", {"points": [v(-5.16, 14.07) * mm, v(-5.47, 14.93) * mm, v(-5.65, 15.87) * mm, v(-5.65, 16.86) * mm]});
            skFitSpline(sketch, "E269", {"points": [v(-5.65, 16.86) * mm, v(-5.65, 18.14) * mm, v(-5.4, 18.71) * mm, v(-5.16, 19.93) * mm]});
            skFitSpline(sketch, "E270", {"points": [v(-5.16, 19.93) * mm, v(-6.86, 18.23) * mm, v(-7.35, 15.64) * mm, v(-7.35, 12.5) * mm]});
            skFitSpline(sketch, "E271", {"points": [v(-7.35, 12.5) * mm, v(-7.35, 12.37) * mm, v(-7.35, 12.24) * mm, v(-7.34, 12.1) * mm]});
            skFitSpline(sketch, "E272", {"points": [v(-7.34, 12.1) * mm, v(-7.84, 11.9) * mm, v(-8.57, 13.11) * mm, v(-9.05, 14.09) * mm]});
            skFitSpline(sketch, "E273", {"points": [v(-9.05, 14.09) * mm, v(-9.05, 10.92) * mm, v(-7.35, 10.92) * mm, v(-7.62, 8.7) * mm]});
            skFitSpline(sketch, "E274", {"points": [v(-7.62, 8.7) * mm, v(-7.1, 8.73) * mm, v(-6.86, 8.97) * mm, v(-6.51, 9.33) * mm]});
            skFitSpline(sketch, "E275", {"points": [v(-6.51, 9.33) * mm, v(-6.23, 8.83) * mm, v(-5.9, 8.37) * mm, v(-5.5, 7.95) * mm]});
            skFitSpline(sketch, "E276", {"points": [v(-5.5, 7.95) * mm, v(-5.78, 6.96) * mm, v(-6.17, 6.02) * mm, v(-6.65, 5.17) * mm]});
            skFitSpline(sketch, "E277", {"points": [v(-6.65, 5.17) * mm, v(-7.99, 5.73) * mm, v(-8.99, 6.97) * mm, v(-9.24, 8.47) * mm]});
            skFitSpline(sketch, "E278", {"points": [v(-9.24, 8.47) * mm, v(-9.28, 8.09) * mm, v(-9.3, 7.69) * mm, v(-9.3, 7.27) * mm]});
            skFitSpline(sketch, "E279", {"points": [v(-9.3, 7.27) * mm, v(-9.3, 5.44) * mm, v(-8.89, 3.83) * mm, v(-8.26, 2.92) * mm]});
            skFitSpline(sketch, "E280", {"points": [v(-8.26, 2.92) * mm, v(-10, 1.02) * mm, v(-12.3, -0.17) * mm, v(-14.8, -0.27) * mm]});
            skFitSpline(sketch, "E281", {"points": [v(-14.8, -0.27) * mm, v(-14.14, -0.43) * mm, v(-13.43, -0.52) * mm, v(-12.7, -0.52) * mm]});
            skFitSpline(sketch, "E282", {"points": [v(-12.7, -0.52) * mm, v(-10.44, -0.52) * mm, v(-8.4, 0.33) * mm, v(-7.02, 1.66) * mm]});
            skFitSpline(sketch, "E283", {"points": [v(-7.02, 1.66) * mm, v(-7.35, 0.72) * mm, v(-7.81, -0.15) * mm, v(-8.4, -0.88) * mm]});
            skFitSpline(sketch, "E284", {"points": [v(-8.4, -0.88) * mm, v(-7.06, -0.23) * mm, v(-5.96, 0.7) * mm, v(-5.08, 1.87) * mm]});
            skFitSpline(sketch, "E285", {"points": [v(-5.08, 1.87) * mm, v(-3.36, 0.95) * mm, v(-1.6, 0.35) * mm, v(0.2, 0.08) * mm]});
            skFitSpline(sketch, "E286", {"points": [v(0.2, 0.08) * mm, v(2, 0.35) * mm, v(3.75, 0.95) * mm, v(5.47, 1.87) * mm]});
            skFitSpline(sketch, "E287", {"points": [v(5.47, 1.87) * mm, v(6.35, 0.7) * mm, v(7.45, -0.23) * mm, v(8.78, -0.88) * mm]});
            skFitSpline(sketch, "E288", {"points": [v(0.2, 3.01) * mm, v(-0.51, 3.57) * mm, v(-1.02, 5.08) * mm, v(-1.02, 6.85) * mm]});
            skFitSpline(sketch, "E289", {"points": [v(-1.02, 6.85) * mm, v(-1.02, 8.62) * mm, v(-0.51, 10.12) * mm, v(0.2, 10.68) * mm]});
            skFitSpline(sketch, "E290", {"points": [v(0.2, 10.68) * mm, v(0.9, 10.12) * mm, v(1.41, 8.62) * mm, v(1.41, 6.85) * mm]});
            skFitSpline(sketch, "E291", {"points": [v(1.41, 6.85) * mm, v(1.41, 5.08) * mm, v(0.9, 3.57) * mm, v(0.2, 3.01) * mm]});
            skLineSegment(sketch, "E292", {"start": v(-5.5, 7.95) * mm, "end": v(-3, 10.18) * mm});
            skLineSegment(sketch, "E293", {"start": v(3.38, 10.18) * mm, "end": v(5.88, 7.95) * mm});
            skLineSegment(sketch, "E294", {"start": v(-5.08, 1.87) * mm, "end": v(-6.65, 5.17) * mm});
            skLineSegment(sketch, "E295", {"start": v(5.47, 1.87) * mm, "end": v(7.04, 5.17) * mm});
            skSolve(sketch);
        }
        {
            var Q0;
            Q0=makeQuery(id+"F14.imprint","IMPRINT",FACE,{"disambiguationData":[TD([[makeQuery(id+"F14.imprint","IMPRINT",EDGE,{"derivedFrom":sQuery(id+"F14.wireOp",EDGE,"E267")}),1.0]])]});
            var Q1;
            Q1=makeQuery(id+"F14.imprint","IMPRINT",FACE,{"disambiguationData":[TD([[makeQuery(id+"F14.imprint","IMPRINT",EDGE,{"derivedFrom":sQuery(id+"F14.wireOp",EDGE,"E238")}),1.0]])]});
            var Q2;
            Q2=makeQuery(id+"F14.imprint","IMPRINT",FACE,{"disambiguationData":[TD([[makeQuery(id+"F14.imprint","IMPRINT",EDGE,{"derivedFrom":sQuery(id+"F14.wireOp",EDGE,"E237")}),1.0]])]});
            extrude(context, id + "F15", {"entities" : qUnion([Q0, Q1, Q2]), "operationType" : NewBodyOperationType.REMOVE, "oppositeDirection" : true, "depth" : 2.5 * mm, "offsetDistance" : 25 * mm});
        }
        {
            var Q0;
            Q0=makeQuery(id+"F14.imprint","IMPRINT",FACE,{"disambiguationData":[TD([[makeQuery(id+"F14.imprint","IMPRINT",EDGE,{"derivedFrom":sQuery(id+"F14.wireOp",EDGE,"E277")}),1.0]])]});
            var Q1;
            Q1=makeQuery(id+"F14.imprint","IMPRINT",FACE,{"disambiguationData":[TD([[makeQuery(id+"F14.imprint","IMPRINT",EDGE,{"derivedFrom":sQuery(id+"F14.wireOp",EDGE,"E230")}),1.0]])]});
            extrude(context, id + "F16", {"entities" : qUnion([Q0, Q1]), "operationType" : NewBodyOperationType.REMOVE, "oppositeDirection" : true, "depth" : 2 * mm, "offsetDistance" : 25 * mm});
        }
        {
            var Q0;
            Q0=makeQuery(id+"F7.boolean.opBoolean","COPY",FACE,{"derivedFrom":makeQuery(id+"F7.opLoft","SWEPT_FACE",FACE,{"disambiguationData":[OSD([sQuery(id+"F6.wireOp",EDGE,"E7.0"),sQuery(id+"F6.wireOp",EDGE,"E7.2"),sQuery(id+"F6.wireOp",EDGE,"E7.3")])]})});
            var sketch = newSketch(context, id + "F17", { "sketchPlane" : qUnion([Q0])});
            skFitSpline(sketch, "E296", {"points": [v(0, 23.34) * mm, v(-9.66, 23.34) * mm, v(-17.5, 15.5) * mm, v(-17.5, 5.84) * mm]});
            skFitSpline(sketch, "E297", {"points": [v(-17.5, 5.84) * mm, v(-17.5, -3.82) * mm, v(-9.66, -11.66) * mm, v(0, -11.66) * mm]});
            skFitSpline(sketch, "E298", {"points": [v(0, -11.66) * mm, v(9.66, -11.66) * mm, v(17.5, -3.82) * mm, v(17.5, 5.84) * mm]});
            skFitSpline(sketch, "E299", {"points": [v(17.5, 5.84) * mm, v(17.5, 15.5) * mm, v(9.66, 23.34) * mm, v(0, 23.34) * mm]});
            skFitSpline(sketch, "E300", {"points": [v(0, 21.54) * mm, v(8.66, 21.54) * mm, v(15.7, 14.5) * mm, v(15.7, 5.84) * mm]});
            skFitSpline(sketch, "E301", {"points": [v(15.7, 5.84) * mm, v(15.7, -2.82) * mm, v(8.66, -9.85) * mm, v(0, -9.85) * mm]});
            skFitSpline(sketch, "E302", {"points": [v(0, -9.85) * mm, v(-8.66, -9.85) * mm, v(-15.7, -2.82) * mm, v(-15.7, 5.84) * mm]});
            skFitSpline(sketch, "E303", {"points": [v(-15.7, 5.84) * mm, v(-15.7, 14.5) * mm, v(-8.66, 21.54) * mm, v(0, 21.54) * mm]});
            skFitSpline(sketch, "E304", {"points": [v(-0.58, 20.56) * mm, v(-4.2, 20.42) * mm, v(-7.5, 18.96) * mm, v(-10, 16.66) * mm]});
            skFitSpline(sketch, "E305", {"points": [v(-5.15, 11.81) * mm, v(-3.83, 12.96) * mm, v(-2.3, 13.6) * mm, v(-0.58, 13.7) * mm]});
            skLineSegment(sketch, "E306", {"start": v(-10, 16.66) * mm, "end": v(-5.15, 11.81) * mm});
            skLineSegment(sketch, "E307", {"start": v(-0.58, 13.7) * mm, "end": v(-0.58, 20.56) * mm});
            skFitSpline(sketch, "E308", {"points": [v(0.58, 17.32) * mm, v(3.31, 17.2) * mm, v(5.69, 16.21) * mm, v(7.7, 14.37) * mm]});
            skLineSegment(sketch, "E309", {"start": v(0.58, 20.56) * mm, "end": v(0.58, 17.32) * mm});
            skFitSpline(sketch, "E310", {"points": [v(9.99, 16.66) * mm, v(7.5, 18.96) * mm, v(4.2, 20.41) * mm, v(0.58, 20.56) * mm]});
            skLineSegment(sketch, "E311", {"start": v(7.7, 14.37) * mm, "end": v(9.99, 16.66) * mm});
            skFitSpline(sketch, "E312", {"points": [v(0.58, 11.87) * mm, v(1.82, 11.77) * mm, v(2.92, 11.31) * mm, v(3.86, 10.52) * mm]});
            skLineSegment(sketch, "E313", {"start": v(0.58, 16.16) * mm, "end": v(0.58, 11.87) * mm});
            skFitSpline(sketch, "E314", {"points": [v(6.88, 13.55) * mm, v(5.2, 15.06) * mm, v(3, 16.03) * mm, v(0.58, 16.16) * mm]});
            skLineSegment(sketch, "E315", {"start": v(3.86, 10.52) * mm, "end": v(6.88, 13.55) * mm});
            skFitSpline(sketch, "E316", {"points": [v(-10.82, 15.84) * mm, v(-13.12, 13.34) * mm, v(-14.57, 10.05) * mm, v(-14.71, 6.42) * mm]});
            skFitSpline(sketch, "E317", {"points": [v(-13.02, 6.42) * mm, v(-12.9, 9.57) * mm, v(-11.76, 12.33) * mm, v(-9.62, 14.64) * mm]});
            skLineSegment(sketch, "E318", {"start": v(-14.71, 6.42) * mm, "end": v(-13.02, 6.42) * mm});
            skLineSegment(sketch, "E319", {"start": v(-9.62, 14.64) * mm, "end": v(-10.82, 15.84) * mm});
            skFitSpline(sketch, "E320", {"points": [v(7.83, 12.85) * mm, v(9.48, 11.03) * mm, v(10.37, 8.88) * mm, v(10.5, 6.42) * mm]});
            skLineSegment(sketch, "E321", {"start": v(10.81, 15.83) * mm, "end": v(7.83, 12.85) * mm});
            skFitSpline(sketch, "E322", {"points": [v(14.71, 6.42) * mm, v(14.57, 10.05) * mm, v(13.12, 13.34) * mm, v(10.81, 15.83) * mm]});
            skLineSegment(sketch, "E323", {"start": v(10.5, 6.42) * mm, "end": v(14.71, 6.42) * mm});
            skFitSpline(sketch, "E324", {"points": [v(-8.79, 13.8) * mm, v(-10.7, 11.73) * mm, v(-11.73, 9.24) * mm, v(-11.84, 6.42) * mm]});
            skFitSpline(sketch, "E325", {"points": [v(-3.45, 6.42) * mm, v(-3.36, 6.96) * mm, v(-3.15, 7.45) * mm, v(-2.85, 7.87) * mm]});
            skLineSegment(sketch, "E326", {"start": v(-11.84, 6.42) * mm, "end": v(-3.45, 6.42) * mm});
            skFitSpline(sketch, "E327", {"points": [v(-0.58, 12.56) * mm, v(-1.99, 12.45) * mm, v(-3.25, 11.93) * mm, v(-4.33, 11) * mm]});
            skLineSegment(sketch, "E328", {"start": v(-2.85, 7.87) * mm, "end": v(-8.79, 13.8) * mm});
            skFitSpline(sketch, "E329", {"points": [v(-2.03, 8.7) * mm, v(-1.6, 9) * mm, v(-1.11, 9.2) * mm, v(-0.58, 9.29) * mm]});
            skLineSegment(sketch, "E330", {"start": v(-4.33, 11) * mm, "end": v(-2.03, 8.7) * mm});
            skLineSegment(sketch, "E331", {"start": v(-0.58, 9.29) * mm, "end": v(-0.58, 12.56) * mm});
            skFitSpline(sketch, "E332", {"points": [v(2.85, 7.87) * mm, v(3.15, 7.45) * mm, v(3.36, 6.96) * mm, v(3.45, 6.42) * mm]});
            skLineSegment(sketch, "E333", {"start": v(7.02, 12.04) * mm, "end": v(2.85, 7.87) * mm});
            skFitSpline(sketch, "E334", {"points": [v(9.35, 6.42) * mm, v(9.22, 8.57) * mm, v(8.36, 10.52) * mm, v(7.02, 12.04) * mm]});
            skLineSegment(sketch, "E335", {"start": v(3.45, 6.42) * mm, "end": v(9.35, 6.42) * mm});
            skFitSpline(sketch, "E336", {"points": [v(0.58, 9.29) * mm, v(1.11, 9.2) * mm, v(1.6, 9) * mm, v(2.03, 8.7) * mm]});
            skLineSegment(sketch, "E337", {"start": v(0.58, 10.7) * mm, "end": v(0.58, 9.29) * mm});
            skFitSpline(sketch, "E338", {"points": [v(3.02, 9.68) * mm, v(2.31, 10.25) * mm, v(1.5, 10.6) * mm, v(0.58, 10.7) * mm]});
            skLineSegment(sketch, "E339", {"start": v(2.03, 8.7) * mm, "end": v(3.02, 9.68) * mm});
            skFitSpline(sketch, "E340", {"points": [v(0, 8.17) * mm, v(-1.29, 8.17) * mm, v(-2.33, 7.13) * mm, v(-2.33, 5.84) * mm]});
            skFitSpline(sketch, "E341", {"points": [v(-2.33, 5.84) * mm, v(-2.33, 4.56) * mm, v(-1.29, 3.51) * mm, v(0, 3.51) * mm]});
            skFitSpline(sketch, "E342", {"points": [v(0, 3.51) * mm, v(1.29, 3.51) * mm, v(2.33, 4.56) * mm, v(2.33, 5.84) * mm]});
            skFitSpline(sketch, "E343", {"points": [v(2.33, 5.84) * mm, v(2.33, 7.13) * mm, v(1.29, 8.17) * mm, v(0, 8.17) * mm]});
            skFitSpline(sketch, "E344", {"points": [v(-14.71, 5.26) * mm, v(-14.57, 1.64) * mm, v(-13.12, -1.65) * mm, v(-10.81, -4.15) * mm]});
            skFitSpline(sketch, "E345", {"points": [v(-6.89, -0.22) * mm, v(-8.29, 1.35) * mm, v(-9.05, 3.2) * mm, v(-9.16, 5.26) * mm]});
            skLineSegment(sketch, "E346", {"start": v(-10.81, -4.15) * mm, "end": v(-6.89, -0.22) * mm});
            skFitSpline(sketch, "E347", {"points": [v(-7.98, 5.26) * mm, v(-7.88, 3.51) * mm, v(-7.23, 1.95) * mm, v(-6.06, 0.61) * mm]});
            skLineSegment(sketch, "E348", {"start": v(-9.16, 5.26) * mm, "end": v(-14.71, 5.26) * mm});
            skFitSpline(sketch, "E349", {"points": [v(-5.62, 1.05) * mm, v(-6.67, 2.26) * mm, v(-7.26, 3.68) * mm, v(-7.36, 5.26) * mm]});
            skLineSegment(sketch, "E350", {"start": v(-6.06, 0.61) * mm, "end": v(-5.62, 1.05) * mm});
            skFitSpline(sketch, "E351", {"points": [v(-6.21, 5.26) * mm, v(-6.1, 4) * mm, v(-5.63, 2.85) * mm, v(-4.8, 1.87) * mm]});
            skLineSegment(sketch, "E352", {"start": v(-7.36, 5.26) * mm, "end": v(-7.98, 5.26) * mm});
            skFitSpline(sketch, "E353", {"points": [v(-2.85, 3.82) * mm, v(-3.15, 4.24) * mm, v(-3.36, 4.73) * mm, v(-3.45, 5.26) * mm]});
            skLineSegment(sketch, "E354", {"start": v(-4.8, 1.87) * mm, "end": v(-2.85, 3.82) * mm});
            skFitSpline(sketch, "E355", {"points": [v(3.45, 5.26) * mm, v(3.36, 4.73) * mm, v(3.15, 4.24) * mm, v(2.85, 3.82) * mm]});
            skLineSegment(sketch, "E356", {"start": v(-3.45, 5.26) * mm, "end": v(-6.21, 5.26) * mm});
            skFitSpline(sketch, "E357", {"points": [v(8.02, -1.35) * mm, v(9.61, 0.42) * mm, v(10.63, 2.72) * mm, v(10.76, 5.26) * mm]});
            skLineSegment(sketch, "E358", {"start": v(2.85, 3.82) * mm, "end": v(8.02, -1.35) * mm});
            skFitSpline(sketch, "E359", {"points": [v(11.85, 5.26) * mm, v(11.72, 2.43) * mm, v(10.7, -0.03) * mm, v(8.79, -2.12) * mm]});
            skLineSegment(sketch, "E360", {"start": v(10.76, 5.26) * mm, "end": v(3.45, 5.26) * mm});
            skFitSpline(sketch, "E361", {"points": [v(9.4, -2.72) * mm, v(11.33, -0.6) * mm, v(12.57, 2.19) * mm, v(12.7, 5.26) * mm]});
            skLineSegment(sketch, "E362", {"start": v(8.79, -2.12) * mm, "end": v(9.4, -2.72) * mm});
            skFitSpline(sketch, "E363", {"points": [v(13.82, 5.26) * mm, v(13.7, 1.88) * mm, v(12.48, -1.04) * mm, v(10.18, -3.52) * mm]});
            skLineSegment(sketch, "E364", {"start": v(12.7, 5.26) * mm, "end": v(11.85, 5.26) * mm});
            skFitSpline(sketch, "E365", {"points": [v(10.81, -4.14) * mm, v(13.11, -1.65) * mm, v(14.57, 1.64) * mm, v(14.71, 5.26) * mm]});
            skLineSegment(sketch, "E366", {"start": v(10.18, -3.52) * mm, "end": v(10.81, -4.14) * mm});
            skLineSegment(sketch, "E367", {"start": v(14.71, 5.26) * mm, "end": v(13.82, 5.26) * mm});
            skFitSpline(sketch, "E368", {"points": [v(-7.98, -2.96) * mm, v(-5.9, -4.88) * mm, v(-3.4, -5.92) * mm, v(-0.58, -6.03) * mm]});
            skLineSegment(sketch, "E369", {"start": v(-2.03, 3) * mm, "end": v(-7.98, -2.96) * mm});
            skFitSpline(sketch, "E370", {"points": [v(-0.58, 2.4) * mm, v(-1.11, 2.49) * mm, v(-1.6, 2.7) * mm, v(-2.03, 3) * mm]});
            skLineSegment(sketch, "E371", {"start": v(-0.58, -6.03) * mm, "end": v(-0.58, 2.4) * mm});
            skFitSpline(sketch, "E372", {"points": [v(2.03, 3) * mm, v(1.6, 2.7) * mm, v(1.11, 2.49) * mm, v(0.58, 2.4) * mm]});
            skFitSpline(sketch, "E373", {"points": [v(0.58, -0.82) * mm, v(2, -0.7) * mm, v(3.27, -0.14) * mm, v(4.3, 0.72) * mm]});
            skLineSegment(sketch, "E374", {"start": v(0.58, 2.4) * mm, "end": v(0.58, -0.82) * mm});
            skFitSpline(sketch, "E375", {"points": [v(5.08, -0.07) * mm, v(3.79, -1.2) * mm, v(2.27, -1.83) * mm, v(0.58, -1.93) * mm]});
            skLineSegment(sketch, "E376", {"start": v(4.3, 0.72) * mm, "end": v(2.03, 3) * mm});
            skFitSpline(sketch, "E377", {"points": [v(0.58, -8.87) * mm, v(4.2, -8.72) * mm, v(7.5, -7.27) * mm, v(9.99, -4.97) * mm]});
            skLineSegment(sketch, "E378", {"start": v(0.58, -1.93) * mm, "end": v(0.58, -8.87) * mm});
            skLineSegment(sketch, "E379", {"start": v(9.99, -4.97) * mm, "end": v(5.08, -0.07) * mm});
            skFitSpline(sketch, "E380", {"points": [v(-9.99, -4.97) * mm, v(-7.5, -7.27) * mm, v(-4.2, -8.73) * mm, v(-0.58, -8.87) * mm]});
            skLineSegment(sketch, "E381", {"start": v(-8.82, -3.8) * mm, "end": v(-9.99, -4.97) * mm});
            skFitSpline(sketch, "E382", {"points": [v(-0.58, -7.2) * mm, v(-3.73, -7.1) * mm, v(-6.5, -5.94) * mm, v(-8.82, -3.8) * mm]});
            skLineSegment(sketch, "E383", {"start": v(-0.58, -8.87) * mm, "end": v(-0.58, -7.2) * mm});
            skLineSegment(sketch, "E384", {"start": v(-40.25, -23.8) * mm, "end": v(0, 47.36) * mm, "construction": true});
            skLineSegment(sketch, "E385", {"start": v(0, 47.36) * mm, "end": v(41.75, -23.8) * mm, "construction": true});
            skLineSegment(sketch, "E386", {"start": v(41.75, -23.8) * mm, "end": v(-40.25, -23.8) * mm, "construction": true});
            skLineSegment(sketch, "E387.0", {"start": v(0, 42.13) * mm, "end": v(29.25, -7.73) * mm});
            skLineSegment(sketch, "E388", {"start": v(-28.2, -7.73) * mm, "end": v(-11.05, -7.73) * mm});
            skLineSegment(sketch, "E389.trimOffspring", {"start": v(-28.2, -7.73) * mm, "end": v(0, 42.13) * mm});
            skLineSegment(sketch, "E390.trimOffspring", {"start": v(11.05, -7.73) * mm, "end": v(29.25, -7.73) * mm});
            skSolve(sketch);
        }
        {
            var Q0;
            Q0=makeQuery(id+"F17.imprint","IMPRINT",FACE,{"disambiguationData":[TD([[makeQuery(id+"F17.imprint","IMPRINT",EDGE,{"derivedFrom":sQuery(id+"F17.wireOp",EDGE,"E300")}),-1.0]])]});
            var Q1;
            {var subQ4=sQuery(id+"F17.wireOp",EDGE,"E296");Q1=makeQuery(id+"F17.imprint","IMPRINT",FACE,{"disambiguationData":[TD([[makeQuery(id+"F17.imprint","IMPRINT",EDGE,{"derivedFrom":subQ4}),-1.0]])]});}
            extrude(context, id + "F18", {"entities" : qUnion([Q0, Q1]), "operationType" : NewBodyOperationType.REMOVE, "oppositeDirection" : true, "depth" : 2 * mm, "offsetDistance" : 25 * mm});
        }
        {
            var Q0;
            Q0=makeQuery(id+"F17.imprint","IMPRINT",FACE,{"disambiguationData":[TD([[makeQuery(id+"F17.imprint","IMPRINT",EDGE,{"derivedFrom":sQuery(id+"F17.wireOp",EDGE,"E316")}),1.0]])]});
            var Q1;
            Q1=makeQuery(id+"F17.imprint","IMPRINT",FACE,{"disambiguationData":[TD([[makeQuery(id+"F17.imprint","IMPRINT",EDGE,{"derivedFrom":sQuery(id+"F17.wireOp",EDGE,"E347")}),1.0]])]});
            var Q2;
            Q2=makeQuery(id+"F17.imprint","IMPRINT",FACE,{"disambiguationData":[TD([[makeQuery(id+"F17.imprint","IMPRINT",EDGE,{"derivedFrom":sQuery(id+"F17.wireOp",EDGE,"E336")}),1.0]])]});
            var Q3;
            Q3=makeQuery(id+"F17.imprint","IMPRINT",FACE,{"disambiguationData":[TD([[makeQuery(id+"F17.imprint","IMPRINT",EDGE,{"derivedFrom":sQuery(id+"F17.wireOp",EDGE,"E359")}),1.0]])]});
            var Q4;
            Q4=makeQuery(id+"F17.imprint","IMPRINT",FACE,{"disambiguationData":[TD([[makeQuery(id+"F17.imprint","IMPRINT",EDGE,{"derivedFrom":sQuery(id+"F17.wireOp",EDGE,"E363")}),1.0]])]});
            var Q5;
            Q5=makeQuery(id+"F17.imprint","IMPRINT",FACE,{"disambiguationData":[TD([[makeQuery(id+"F17.imprint","IMPRINT",EDGE,{"derivedFrom":sQuery(id+"F17.wireOp",EDGE,"E372")}),1.0]])]});
            var Q6;
            Q6=makeQuery(id+"F17.imprint","IMPRINT",FACE,{"disambiguationData":[TD([[makeQuery(id+"F17.imprint","IMPRINT",EDGE,{"derivedFrom":sQuery(id+"F17.wireOp",EDGE,"E351")}),1.0]])]});
            var Q7;
            Q7=makeQuery(id+"F17.imprint","IMPRINT",FACE,{"disambiguationData":[TD([[makeQuery(id+"F17.imprint","IMPRINT",EDGE,{"derivedFrom":sQuery(id+"F17.wireOp",EDGE,"E327")}),1.0]])]});
            var Q8;
            Q8=makeQuery(id+"F17.imprint","IMPRINT",FACE,{"disambiguationData":[TD([[makeQuery(id+"F17.imprint","IMPRINT",EDGE,{"derivedFrom":sQuery(id+"F17.wireOp",EDGE,"E380")}),1.0]])]});
            var Q9;
            Q9=makeQuery(id+"F17.imprint","IMPRINT",FACE,{"disambiguationData":[TD([[makeQuery(id+"F17.imprint","IMPRINT",EDGE,{"derivedFrom":sQuery(id+"F17.wireOp",EDGE,"E340")}),1.0]])]});
            var Q10;
            Q10=makeQuery(id+"F17.imprint","IMPRINT",FACE,{"disambiguationData":[TD([[makeQuery(id+"F17.imprint","IMPRINT",EDGE,{"derivedFrom":sQuery(id+"F17.wireOp",EDGE,"E308")}),1.0]])]});
            var Q11;
            Q11=makeQuery(id+"F17.imprint","IMPRINT",FACE,{"disambiguationData":[TD([[makeQuery(id+"F17.imprint","IMPRINT",EDGE,{"derivedFrom":sQuery(id+"F17.wireOp",EDGE,"E332")}),1.0]])]});
            extrude(context, id + "F19", {"entities" : qUnion([Q0, Q1, Q2, Q3, Q4, Q5, Q6, Q7, Q8, Q9, Q10, Q11]), "operationType" : NewBodyOperationType.REMOVE, "oppositeDirection" : true, "depth" : 2.75 * mm, "offsetDistance" : 25 * mm});
        }
        {
            var Q0;
            Q0=makeQuery(id+"F12.imprint","IMPRINT",FACE,{"disambiguationData":[TD([[makeQuery(id+"F12.imprint","IMPRINT",EDGE,{"derivedFrom":sQuery(id+"F12.wireOp",EDGE,"E168.0")}),-1.0]])]});
            extrude(context, id + "F20", {"entities" : qUnion([Q0]), "operationType" : NewBodyOperationType.REMOVE, "oppositeDirection" : true, "depth" : 1 * mm, "offsetDistance" : 25 * mm});
        }
        {
            var Q0;
            Q0=makeQuery(id+"F14.imprint","IMPRINT",FACE,{"disambiguationData":[TD([[makeQuery(id+"F14.imprint","IMPRINT",EDGE,{"derivedFrom":sQuery(id+"F14.wireOp",EDGE,"E227.0")}),-1.0]])]});
            extrude(context, id + "F21", {"entities" : qUnion([Q0]), "operationType" : NewBodyOperationType.REMOVE, "oppositeDirection" : true, "depth" : 1 * mm, "offsetDistance" : 25 * mm});
        }
    });
